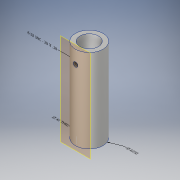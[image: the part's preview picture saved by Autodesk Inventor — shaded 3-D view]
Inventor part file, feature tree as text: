
AUTODESK INVENTOR PART (.ipt)
format: ipt  version: 2018.3 (Build 223284000, 284)  size: 128,512 bytes
history: native  units: in
note: dims shown in document units (in); Inventor stores cm internally (conversion verified against a paired STEP export)
features: hole x4, other x2, sketch x2, extrude x1, plane x1
ambient origin geometry x8: Origin, YZ Plane, XZ Plane, XY Plane, X Axis, Y Axis, Z Axis, Center Point
bodies: Solid1 (feature_tree)
feature tree (10):
  other  "Annotations"
  extrude  "Extrusion1"  Depth=1.0in
  hole  "Hole1"  [1 undecoded]
  plane  "Work Plane1"
  hole  "Hole2"  [1 undecoded]
  sketch  "Sketch1"  dims[d0=1.9in d1=0.0in d38=1.0in d39=1.0in]
  sketch  "Sketch2"  dims[d5=0.5in d6=0.119in d7=0.25in d8=0.5635in d9=1.9in d10=0.8108in d11=1.6in d12=0.104in d13=0.276in d14=0.375in d15=0.25in d16=0.5635in d17=0.3in d18=0.8108in d23=0.0in d25=2.4591in d26=0.3358in d27=0.3804in d29=2.3209in d30=0.625in]
  hole  "Hole Note 1"  [1 undecoded]
  hole  "Hole Note 2"  [1 undecoded]
  other  "Diameter Dimension 1"
note: 4 required parameter values undecoded (feature->parameter linkage not recoverable at this tier; creation-order binding heuristic only, values carry confidence <= 0.55)
